# Revit family: QF_COMCATER ALL BRANDS_RCP4
name_source: partatom
category: Specialty Equipment
revit_build: Autodesk Revit 2014 (Build: 20140709_2115(x64)
units: mm (PartAtom-declared; Revit-internal decimal feet)

## types (2) — shared parameters
Accessory = No
Assembly Code = E1090320
BTUH = 9500 W
Cold Water Flow = 0.0 L/s
Cold Water Size = 13 mm
Cold Water Temperature Recommended = 0 °C
Depth Actual = 803 mm  [stored 2.63451 ft]
Description = PASTA COOKER
Gas Flow = 0.0 L/s
Gas Size = 19 mm
Gas Size Flexible = 0 mm
Gas power kW = 9.5
Height Actual = 1135 mm
Indirect Waste Size = 32 mm
Length Actual = 400 mm  [stored 1.31234 ft]
Manufacturer = TRUEHEAT
Model = RCP4
Nominal Gas power = 9500 W
Type Comments = The Australian owned and designed* Trueheat RC Series of Gas Cooking Equipment has been developed for the restaurant and cafe market with a high quality finish, designed to fulfill the busy demands within a commercial kitchen.
High grade 316 grade stainless steel pot. 35 litre capacity.
Cast iron H burner. No electrical power required.

## type names (no varying parameters)
- RCP4_Natural Gas
- RCP4_LPG

note: [stored X ft] marks values corroborated as IEEE doubles in the binary element streams (Revit-internal decimal feet)

## geometry (parser evidence)
native form markers: Sweep x5
no freeform markers — native parametric forms only
